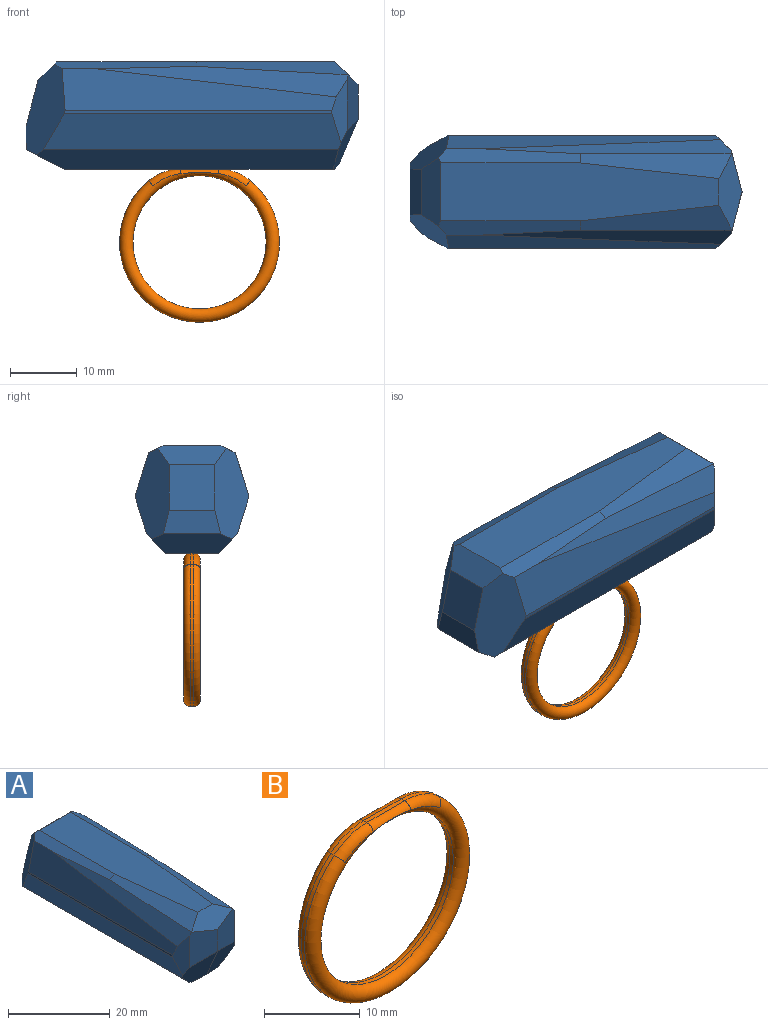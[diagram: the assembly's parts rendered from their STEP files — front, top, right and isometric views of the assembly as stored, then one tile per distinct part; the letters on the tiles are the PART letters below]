
ASSEMBLY  parts=2 mates=1
PART A: 33 faces, bbox 17x49.8x16.1 mm
  f0: plane 45.32x2.9mm, normal (0.71,0,-0.71), area 177.5mm2, adj f6,f8,f14,f16,f18
  f1: plane 9.49x2.3mm, normal (0.71,-0.71,0), area 19.1mm2, adj f5,f9,f13,f14,f17,f18
  f2: plane 22.75x3.71mm, normal (0.45,-0.05,0.89), area 63.4mm2, adj f4,f5,f10,f15,f17
  f3: plane 4.82x0.63mm, normal (0,-0.71,-0.71), area 2.1mm2, adj f8,f18,f19
  f4: plane 11.46x3.46mm, normal (0,-0.71,0.71), area 33.7mm2, adj f2,f15,f17,f20,f27
  f5: plane 37.76x4.6mm, normal (0.85,-0.03,0.53), area 91.5mm2, adj f1,f2,f10,f13,f17
  f6: plane 13.6x5.87mm, normal (0.71,0.68,0.18), area 72.8mm2, adj f0,f7,f9,f10,f11,f12,f13,f14
  f7: plane 8.62x3.52mm, normal (0,1,0), area 27.2mm2, adj f6,f12,f16,f25
  f8: plane 40.54x7.84mm, normal (0,0,-1), area 317.6mm2, adj f0,f3,f16,f18,f19,f29
  f9: plane 40.18x0.52mm, normal (1,0,0), area 20.7mm2, adj f1,f6,f13,f14
  f10: plane 21.38x2.14mm, normal (0.45,0,0.89), area 43.8mm2, adj f2,f5,f6,f11,f13,f15
  f11: plane 10.3x2.82mm, normal (0,0.71,0.71), area 34.7mm2, adj f6,f10,f12,f15,f23,f25
  f12: plane 6.88x6.84mm, normal (0,0.97,0.25), area 48.6mm2, adj f6,f7,f11,f25
  f13: plane 41.15x6.24mm, normal (0.95,0,0.31), area 188mm2, adj f1,f5,f6,f9,f10
  f14: plane 44.68x5.39mm, normal (0.95,0,-0.3), area 240mm2, adj f0,f1,f6,f9,f18
  f15: plane 41.76x8.69mm, normal (0,0,1), area 314.6mm2, adj f2,f4,f10,f11,f23,f27
  f16: plane 12.07x5.8mm, normal (0,0.45,-0.89), area 65.3mm2, adj f0,f6,f7,f8,f25,f29
  f17: plane 8.34x6.2mm, normal (0.25,-0.97,0), area 43.6mm2, adj f1,f2,f4,f5,f18,f20
  f18: plane 7.43x7.14mm, normal (0.14,-0.91,-0.39), area 43.4mm2, adj f0,f1,f3,f8,f14,f17,f19
  f19: plane 7.43x7.14mm, normal (-0.14,-0.91,-0.39), area 43.4mm2, adj f3,f8,f18,f20,f21,f28,f29
  f20: plane 8.34x6.2mm, normal (-0.25,-0.97,0), area 43.6mm2, adj f4,f17,f19,f26,f27,f28
  f21: plane 44.68x5.39mm, normal (-0.95,0,-0.3), area 240mm2, adj f19,f24,f25,f28,f29
  f22: plane 41.15x6.24mm, normal (-0.95,0,0.31), area 188mm2, adj f23,f24,f25,f26,f28
  f23: plane 21.38x2.14mm, normal (-0.45,0,0.89), area 43.8mm2, adj f11,f15,f22,f25,f26,f27
  f24: plane 40.18x0.52mm, normal (-1,0,0), area 20.7mm2, adj f21,f22,f25,f28
  f25: plane 13.6x5.87mm, normal (-0.71,0.68,0.18), area 72.8mm2, adj f7,f11,f12,f16,f21,f22,f23,f24
  f26: plane 37.76x4.6mm, normal (-0.85,-0.03,0.53), area 91.5mm2, adj f20,f22,f23,f27,f28
  f27: plane 22.75x3.71mm, normal (-0.45,-0.05,0.89), area 63.4mm2, adj f4,f15,f20,f23,f26
  f28: plane 9.49x2.3mm, normal (-0.71,-0.71,0), area 19.1mm2, adj f19,f20,f21,f22,f24,f26
  f29: plane 45.32x2.9mm, normal (-0.71,0,-0.71), area 177.5mm2, adj f8,f16,f19,f21,f25
  f30: plane 15x15mm, normal (0,1,0), area 176.7mm2, adj f32
  f31: plane 15x15mm, normal (0,-1,0), area 176.7mm2, adj f32
  f32: cylinder r=7.5mm len=40mm, axis (0,1,0), area 1885mm2, adj f30,f31
PART B: 13 faces, bbox 26x2.5x26 mm
  f0: plane 5.57x0.5mm, normal (0,0,1), area 2.8mm2, adj f3,f4,f8,f12
  f1: cylinder r=10mm len=20mm, axis (0,1,0), area 31.4mm2, adj f5,f9
  f2: cylinder r=12mm len=24mm, axis (0,1,0), area 29.4mm2, adj f3,f4,f5,f9
  f3: cylinder r=7.62mm len=4.85mm, axis (0,1,0), area 2.6mm2, adj f0,f2,f7,f10
  f4: cylinder r=7.62mm len=4.85mm, axis (0,1,0), area 2.6mm2, adj f0,f2,f6,f11
  f5: torus R=11mm, axis (0,-1,0), area 187.9mm2, adj f1,f2,f6,f7,f8
  f6: torus R=6.62mm, axis (0,-1,0), area 7.1mm2, adj f4,f5,f8
  f7: torus R=6.62mm, axis (0,-1,0), area 7.1mm2, adj f3,f5,f8
  f8: cylinder r=1mm len=5.57mm, axis (1,0,0), area 6.2mm2, adj f0,f5,f6,f7
  f9: torus R=11mm, axis (0,-1,0), area 187.9mm2, adj f1,f2,f10,f11,f12
  f10: torus R=6.62mm, axis (0,-1,0), area 7.1mm2, adj f3,f9,f12
  f11: torus R=6.62mm, axis (0,-1,0), area 7.1mm2, adj f4,f9,f12
  f12: cylinder r=1mm len=5.57mm, axis (-1,0,0), area 6.2mm2, adj f0,f9,f10,f11
PLACE A rot(axis=(0,0,1),90deg) t=(51.6,29.17,18.45)mm
PLACE B t=(51.65,30.42,-0.63)mm
MATE fastened A.f8 <-> B.f0  axis (0,0,-1) through (51.65,29.17,10.37)mm
